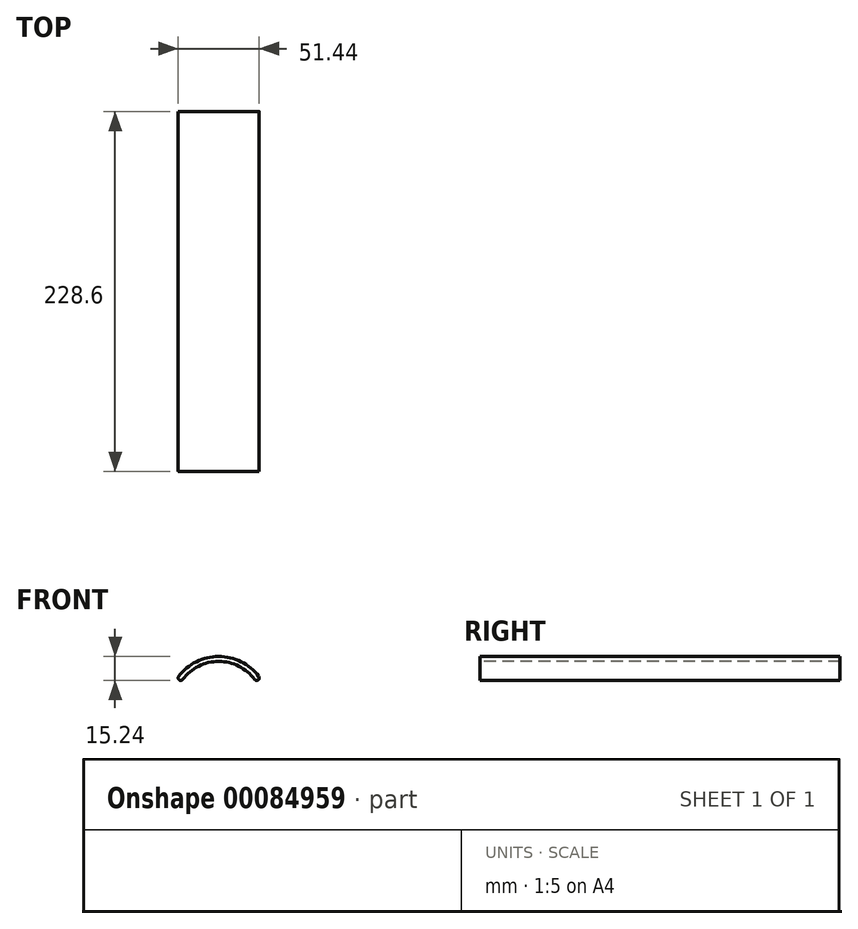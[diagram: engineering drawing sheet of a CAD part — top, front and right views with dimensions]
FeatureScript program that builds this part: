
annotation { "Feature Type Name" : "Feature", "Feature Type Description" : "" }
export const myFeature = defineFeature(function(context is Context, id is Id, definition is map)
    precondition{}
    {
        {
            var Q0;
            Q0=qCreatedBy(makeId("Front.planeOp"),FACE);
            var sketch = newSketch(context, id + "F0", { "sketchPlane" : qUnion([Q0])});
            skArc(sketch, "E0", {"start": v(50.8, 0) * mm, "mid": v(25.4, 12.7) * mm, "end": v(0, 0) * mm});
            skPoint(sketch, "E1", {"position": v(25.4, 12.7) * mm});
            skArc(sketch, "E2.0", {"start": v(48.26, -1.9) * mm, "mid": v(25.4, 9.53) * mm, "end": v(2.54, -1.9) * mm});
            skArc(sketch, "E3", {"start": v(0, 0) * mm, "mid": v(0.32, -2.22) * mm, "end": v(2.54, -1.9) * mm});
            skArc(sketch, "E4", {"start": v(50.8, 0) * mm, "mid": v(50.48, -2.22) * mm, "end": v(48.26, -1.9) * mm});
            skSolve(sketch);
        }
        {
            var Q0;
            Q0=makeQuery(id+"F0.imprint","IMPRINT",FACE,{"disambiguationData":[TD([[makeQuery(id+"F0.imprint","IMPRINT",EDGE,{"derivedFrom":sQuery(id+"F0.wireOp",EDGE,"E0")}),1.0]])]});
            extrude(context, id + "F1", {"entities" : qUnion([Q0]), "oppositeDirection" : true, "depth" : 228.6 * mm});
        }
    });
